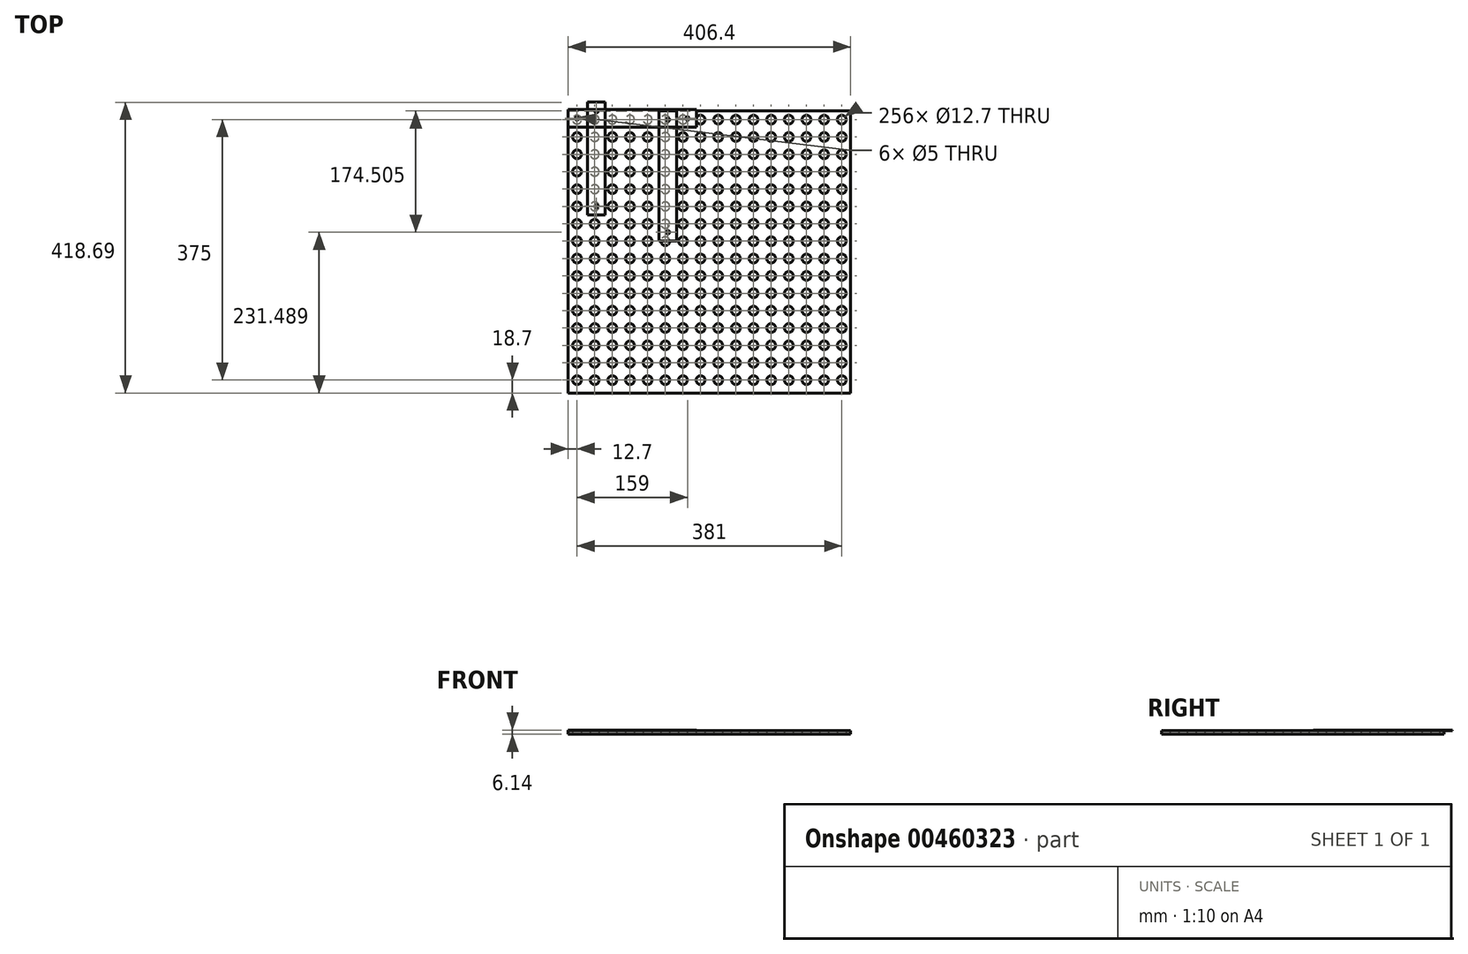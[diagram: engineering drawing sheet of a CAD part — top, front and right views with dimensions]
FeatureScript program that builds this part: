
annotation { "Feature Type Name" : "Feature", "Feature Type Description" : "" }
export const myFeature = defineFeature(function(context is Context, id is Id, definition is map)
    precondition{}
    {
        {
            var Q0;
            Q0=qCreatedBy(makeId("Top.planeOp"),FACE);
            var sketch = newSketch(context, id + "F0", { "sketchPlane" : qUnion([Q0])});
            skLineSegment(sketch, "E0.bottom", {"start": v(6.35, -6.35) * mm, "end": v(412.75, -6.35) * mm});
            skLineSegment(sketch, "E0.top", {"start": v(6.35, 400.05) * mm, "end": v(412.75, 400.05) * mm});
            skLineSegment(sketch, "E0.left", {"start": v(6.35, -6.35) * mm, "end": v(6.35, 400.05) * mm});
            skLineSegment(sketch, "E0.right", {"start": v(412.75, -6.35) * mm, "end": v(412.75, 400.05) * mm});
            skCircle(sketch, "E1", {"center": v(19.05, 387.35) * mm, "radius": 6.35 * mm});
            skLineSegment(sketch, "E2", {"start": v(19.05, 387.35) * mm, "end": v(19.05, 400.05) * mm, "construction": true});
            skLineSegment(sketch, "E3", {"start": v(19.05, 387.35) * mm, "end": v(6.35, 387.35) * mm, "construction": true});
            skCircle(sketch, "E4.0.1.0", {"center": v(19.05, 362.35) * mm, "radius": 6.35 * mm});
            skCircle(sketch, "E4.0.2.0", {"center": v(19.05, 337.35) * mm, "radius": 6.35 * mm});
            skCircle(sketch, "E4.0.3.0", {"center": v(19.05, 312.35) * mm, "radius": 6.35 * mm});
            skCircle(sketch, "E4.0.4.0", {"center": v(19.05, 287.35) * mm, "radius": 6.35 * mm});
            skCircle(sketch, "E4.0.5.0", {"center": v(19.05, 262.35) * mm, "radius": 6.35 * mm});
            skCircle(sketch, "E4.0.6.0", {"center": v(19.05, 237.35) * mm, "radius": 6.35 * mm});
            skCircle(sketch, "E4.0.7.0", {"center": v(19.05, 212.35) * mm, "radius": 6.35 * mm});
            skCircle(sketch, "E4.0.8.0", {"center": v(19.05, 187.35) * mm, "radius": 6.35 * mm});
            skCircle(sketch, "E4.0.9.0", {"center": v(19.05, 162.35) * mm, "radius": 6.35 * mm});
            skCircle(sketch, "E4.0.10.0", {"center": v(19.05, 137.35) * mm, "radius": 6.35 * mm});
            skCircle(sketch, "E4.0.11.0", {"center": v(19.05, 112.35) * mm, "radius": 6.35 * mm});
            skCircle(sketch, "E4.0.12.0", {"center": v(19.05, 87.35) * mm, "radius": 6.35 * mm});
            skCircle(sketch, "E4.0.13.0", {"center": v(19.05, 62.35) * mm, "radius": 6.35 * mm});
            skCircle(sketch, "E4.0.14.0", {"center": v(19.05, 37.35) * mm, "radius": 6.35 * mm});
            skCircle(sketch, "E4.1.0.0", {"center": v(44.45, 387.35) * mm, "radius": 6.35 * mm});
            skCircle(sketch, "E4.1.1.0", {"center": v(44.45, 362.35) * mm, "radius": 6.35 * mm});
            skCircle(sketch, "E4.1.2.0", {"center": v(44.45, 337.35) * mm, "radius": 6.35 * mm});
            skCircle(sketch, "E4.1.3.0", {"center": v(44.45, 312.35) * mm, "radius": 6.35 * mm});
            skCircle(sketch, "E4.1.4.0", {"center": v(44.45, 287.35) * mm, "radius": 6.35 * mm});
            skCircle(sketch, "E4.1.5.0", {"center": v(44.45, 262.35) * mm, "radius": 6.35 * mm});
            skCircle(sketch, "E4.1.6.0", {"center": v(44.45, 237.35) * mm, "radius": 6.35 * mm});
            skCircle(sketch, "E4.1.7.0", {"center": v(44.45, 212.35) * mm, "radius": 6.35 * mm});
            skCircle(sketch, "E4.1.8.0", {"center": v(44.45, 187.35) * mm, "radius": 6.35 * mm});
            skCircle(sketch, "E4.1.9.0", {"center": v(44.45, 162.35) * mm, "radius": 6.35 * mm});
            skCircle(sketch, "E4.1.10.0", {"center": v(44.45, 137.35) * mm, "radius": 6.35 * mm});
            skCircle(sketch, "E4.1.11.0", {"center": v(44.45, 112.35) * mm, "radius": 6.35 * mm});
            skCircle(sketch, "E4.1.12.0", {"center": v(44.45, 87.35) * mm, "radius": 6.35 * mm});
            skCircle(sketch, "E4.1.13.0", {"center": v(44.45, 62.35) * mm, "radius": 6.35 * mm});
            skCircle(sketch, "E4.1.14.0", {"center": v(44.45, 37.35) * mm, "radius": 6.35 * mm});
            skCircle(sketch, "E4.2.0.0", {"center": v(69.85, 387.35) * mm, "radius": 6.35 * mm});
            skCircle(sketch, "E4.2.1.0", {"center": v(69.85, 362.35) * mm, "radius": 6.35 * mm});
            skCircle(sketch, "E4.2.2.0", {"center": v(69.85, 337.35) * mm, "radius": 6.35 * mm});
            skCircle(sketch, "E4.2.3.0", {"center": v(69.85, 312.35) * mm, "radius": 6.35 * mm});
            skCircle(sketch, "E4.2.4.0", {"center": v(69.85, 287.35) * mm, "radius": 6.35 * mm});
            skCircle(sketch, "E4.2.5.0", {"center": v(69.85, 262.35) * mm, "radius": 6.35 * mm});
            skCircle(sketch, "E4.2.6.0", {"center": v(69.85, 237.35) * mm, "radius": 6.35 * mm});
            skCircle(sketch, "E4.2.7.0", {"center": v(69.85, 212.35) * mm, "radius": 6.35 * mm});
            skCircle(sketch, "E4.2.8.0", {"center": v(69.85, 187.35) * mm, "radius": 6.35 * mm});
            skCircle(sketch, "E4.2.9.0", {"center": v(69.85, 162.35) * mm, "radius": 6.35 * mm});
            skCircle(sketch, "E4.2.10.0", {"center": v(69.85, 137.35) * mm, "radius": 6.35 * mm});
            skCircle(sketch, "E4.2.11.0", {"center": v(69.85, 112.35) * mm, "radius": 6.35 * mm});
            skCircle(sketch, "E4.2.12.0", {"center": v(69.85, 87.35) * mm, "radius": 6.35 * mm});
            skCircle(sketch, "E4.2.13.0", {"center": v(69.85, 62.35) * mm, "radius": 6.35 * mm});
            skCircle(sketch, "E4.2.14.0", {"center": v(69.85, 37.35) * mm, "radius": 6.35 * mm});
            skCircle(sketch, "E4.3.0.0", {"center": v(95.25, 387.35) * mm, "radius": 6.35 * mm});
            skCircle(sketch, "E4.3.1.0", {"center": v(95.25, 362.35) * mm, "radius": 6.35 * mm});
            skCircle(sketch, "E4.3.2.0", {"center": v(95.25, 337.35) * mm, "radius": 6.35 * mm});
            skCircle(sketch, "E4.3.3.0", {"center": v(95.25, 312.35) * mm, "radius": 6.35 * mm});
            skCircle(sketch, "E4.3.4.0", {"center": v(95.25, 287.35) * mm, "radius": 6.35 * mm});
            skCircle(sketch, "E4.3.5.0", {"center": v(95.25, 262.35) * mm, "radius": 6.35 * mm});
            skCircle(sketch, "E4.3.6.0", {"center": v(95.25, 237.35) * mm, "radius": 6.35 * mm});
            skCircle(sketch, "E4.3.7.0", {"center": v(95.25, 212.35) * mm, "radius": 6.35 * mm});
            skCircle(sketch, "E4.3.8.0", {"center": v(95.25, 187.35) * mm, "radius": 6.35 * mm});
            skCircle(sketch, "E4.3.9.0", {"center": v(95.25, 162.35) * mm, "radius": 6.35 * mm});
            skCircle(sketch, "E4.3.10.0", {"center": v(95.25, 137.35) * mm, "radius": 6.35 * mm});
            skCircle(sketch, "E4.3.11.0", {"center": v(95.25, 112.35) * mm, "radius": 6.35 * mm});
            skCircle(sketch, "E4.3.12.0", {"center": v(95.25, 87.35) * mm, "radius": 6.35 * mm});
            skCircle(sketch, "E4.3.13.0", {"center": v(95.25, 62.35) * mm, "radius": 6.35 * mm});
            skCircle(sketch, "E4.3.14.0", {"center": v(95.25, 37.35) * mm, "radius": 6.35 * mm});
            skCircle(sketch, "E4.4.0.0", {"center": v(120.65, 387.35) * mm, "radius": 6.35 * mm});
            skCircle(sketch, "E4.4.1.0", {"center": v(120.65, 362.35) * mm, "radius": 6.35 * mm});
            skCircle(sketch, "E4.4.2.0", {"center": v(120.65, 337.35) * mm, "radius": 6.35 * mm});
            skCircle(sketch, "E4.4.3.0", {"center": v(120.65, 312.35) * mm, "radius": 6.35 * mm});
            skCircle(sketch, "E4.4.4.0", {"center": v(120.65, 287.35) * mm, "radius": 6.35 * mm});
            skCircle(sketch, "E4.4.5.0", {"center": v(120.65, 262.35) * mm, "radius": 6.35 * mm});
            skCircle(sketch, "E4.4.6.0", {"center": v(120.65, 237.35) * mm, "radius": 6.35 * mm});
            skCircle(sketch, "E4.4.7.0", {"center": v(120.65, 212.35) * mm, "radius": 6.35 * mm});
            skCircle(sketch, "E4.4.8.0", {"center": v(120.65, 187.35) * mm, "radius": 6.35 * mm});
            skCircle(sketch, "E4.4.9.0", {"center": v(120.65, 162.35) * mm, "radius": 6.35 * mm});
            skCircle(sketch, "E4.4.10.0", {"center": v(120.65, 137.35) * mm, "radius": 6.35 * mm});
            skCircle(sketch, "E4.4.11.0", {"center": v(120.65, 112.35) * mm, "radius": 6.35 * mm});
            skCircle(sketch, "E4.4.12.0", {"center": v(120.65, 87.35) * mm, "radius": 6.35 * mm});
            skCircle(sketch, "E4.4.13.0", {"center": v(120.65, 62.35) * mm, "radius": 6.35 * mm});
            skCircle(sketch, "E4.4.14.0", {"center": v(120.65, 37.35) * mm, "radius": 6.35 * mm});
            skCircle(sketch, "E4.5.0.0", {"center": v(146.05, 387.35) * mm, "radius": 6.35 * mm});
            skCircle(sketch, "E4.5.1.0", {"center": v(146.05, 362.35) * mm, "radius": 6.35 * mm});
            skCircle(sketch, "E4.5.2.0", {"center": v(146.05, 337.35) * mm, "radius": 6.35 * mm});
            skCircle(sketch, "E4.5.3.0", {"center": v(146.05, 312.35) * mm, "radius": 6.35 * mm});
            skCircle(sketch, "E4.5.4.0", {"center": v(146.05, 287.35) * mm, "radius": 6.35 * mm});
            skCircle(sketch, "E4.5.5.0", {"center": v(146.05, 262.35) * mm, "radius": 6.35 * mm});
            skCircle(sketch, "E4.5.6.0", {"center": v(146.05, 237.35) * mm, "radius": 6.35 * mm});
            skCircle(sketch, "E4.5.7.0", {"center": v(146.05, 212.35) * mm, "radius": 6.35 * mm});
            skCircle(sketch, "E4.5.8.0", {"center": v(146.05, 187.35) * mm, "radius": 6.35 * mm});
            skCircle(sketch, "E4.5.9.0", {"center": v(146.05, 162.35) * mm, "radius": 6.35 * mm});
            skCircle(sketch, "E4.5.10.0", {"center": v(146.05, 137.35) * mm, "radius": 6.35 * mm});
            skCircle(sketch, "E4.5.11.0", {"center": v(146.05, 112.35) * mm, "radius": 6.35 * mm});
            skCircle(sketch, "E4.5.12.0", {"center": v(146.05, 87.35) * mm, "radius": 6.35 * mm});
            skCircle(sketch, "E4.5.13.0", {"center": v(146.05, 62.35) * mm, "radius": 6.35 * mm});
            skCircle(sketch, "E4.5.14.0", {"center": v(146.05, 37.35) * mm, "radius": 6.35 * mm});
            skCircle(sketch, "E4.6.0.0", {"center": v(171.45, 387.35) * mm, "radius": 6.35 * mm});
            skCircle(sketch, "E4.6.1.0", {"center": v(171.45, 362.35) * mm, "radius": 6.35 * mm});
            skCircle(sketch, "E4.6.2.0", {"center": v(171.45, 337.35) * mm, "radius": 6.35 * mm});
            skCircle(sketch, "E4.6.3.0", {"center": v(171.45, 312.35) * mm, "radius": 6.35 * mm});
            skCircle(sketch, "E4.6.4.0", {"center": v(171.45, 287.35) * mm, "radius": 6.35 * mm});
            skCircle(sketch, "E4.6.5.0", {"center": v(171.45, 262.35) * mm, "radius": 6.35 * mm});
            skCircle(sketch, "E4.6.6.0", {"center": v(171.45, 237.35) * mm, "radius": 6.35 * mm});
            skCircle(sketch, "E4.6.7.0", {"center": v(171.45, 212.35) * mm, "radius": 6.35 * mm});
            skCircle(sketch, "E4.6.8.0", {"center": v(171.45, 187.35) * mm, "radius": 6.35 * mm});
            skCircle(sketch, "E4.6.9.0", {"center": v(171.45, 162.35) * mm, "radius": 6.35 * mm});
            skCircle(sketch, "E4.6.10.0", {"center": v(171.45, 137.35) * mm, "radius": 6.35 * mm});
            skCircle(sketch, "E4.6.11.0", {"center": v(171.45, 112.35) * mm, "radius": 6.35 * mm});
            skCircle(sketch, "E4.6.12.0", {"center": v(171.45, 87.35) * mm, "radius": 6.35 * mm});
            skCircle(sketch, "E4.6.13.0", {"center": v(171.45, 62.35) * mm, "radius": 6.35 * mm});
            skCircle(sketch, "E4.6.14.0", {"center": v(171.45, 37.35) * mm, "radius": 6.35 * mm});
            skCircle(sketch, "E4.7.0.0", {"center": v(196.85, 387.35) * mm, "radius": 6.35 * mm});
            skCircle(sketch, "E4.7.1.0", {"center": v(196.85, 362.35) * mm, "radius": 6.35 * mm});
            skCircle(sketch, "E4.7.2.0", {"center": v(196.85, 337.35) * mm, "radius": 6.35 * mm});
            skCircle(sketch, "E4.7.3.0", {"center": v(196.85, 312.35) * mm, "radius": 6.35 * mm});
            skCircle(sketch, "E4.7.4.0", {"center": v(196.85, 287.35) * mm, "radius": 6.35 * mm});
            skCircle(sketch, "E4.7.5.0", {"center": v(196.85, 262.35) * mm, "radius": 6.35 * mm});
            skCircle(sketch, "E4.7.6.0", {"center": v(196.85, 237.35) * mm, "radius": 6.35 * mm});
            skCircle(sketch, "E4.7.7.0", {"center": v(196.85, 212.35) * mm, "radius": 6.35 * mm});
            skCircle(sketch, "E4.7.8.0", {"center": v(196.85, 187.35) * mm, "radius": 6.35 * mm});
            skCircle(sketch, "E4.7.9.0", {"center": v(196.85, 162.35) * mm, "radius": 6.35 * mm});
            skCircle(sketch, "E4.7.10.0", {"center": v(196.85, 137.35) * mm, "radius": 6.35 * mm});
            skCircle(sketch, "E4.7.11.0", {"center": v(196.85, 112.35) * mm, "radius": 6.35 * mm});
            skCircle(sketch, "E4.7.12.0", {"center": v(196.85, 87.35) * mm, "radius": 6.35 * mm});
            skCircle(sketch, "E4.7.13.0", {"center": v(196.85, 62.35) * mm, "radius": 6.35 * mm});
            skCircle(sketch, "E4.7.14.0", {"center": v(196.85, 37.35) * mm, "radius": 6.35 * mm});
            skCircle(sketch, "E4.8.0.0", {"center": v(222.25, 387.35) * mm, "radius": 6.35 * mm});
            skCircle(sketch, "E4.8.1.0", {"center": v(222.25, 362.35) * mm, "radius": 6.35 * mm});
            skCircle(sketch, "E4.8.2.0", {"center": v(222.25, 337.35) * mm, "radius": 6.35 * mm});
            skCircle(sketch, "E4.8.3.0", {"center": v(222.25, 312.35) * mm, "radius": 6.35 * mm});
            skCircle(sketch, "E4.8.4.0", {"center": v(222.25, 287.35) * mm, "radius": 6.35 * mm});
            skCircle(sketch, "E4.8.5.0", {"center": v(222.25, 262.35) * mm, "radius": 6.35 * mm});
            skCircle(sketch, "E4.8.6.0", {"center": v(222.25, 237.35) * mm, "radius": 6.35 * mm});
            skCircle(sketch, "E4.8.7.0", {"center": v(222.25, 212.35) * mm, "radius": 6.35 * mm});
            skCircle(sketch, "E4.8.8.0", {"center": v(222.25, 187.35) * mm, "radius": 6.35 * mm});
            skCircle(sketch, "E4.8.9.0", {"center": v(222.25, 162.35) * mm, "radius": 6.35 * mm});
            skCircle(sketch, "E4.8.10.0", {"center": v(222.25, 137.35) * mm, "radius": 6.35 * mm});
            skCircle(sketch, "E4.8.11.0", {"center": v(222.25, 112.35) * mm, "radius": 6.35 * mm});
            skCircle(sketch, "E4.8.12.0", {"center": v(222.25, 87.35) * mm, "radius": 6.35 * mm});
            skCircle(sketch, "E4.8.13.0", {"center": v(222.25, 62.35) * mm, "radius": 6.35 * mm});
            skCircle(sketch, "E4.8.14.0", {"center": v(222.25, 37.35) * mm, "radius": 6.35 * mm});
            skCircle(sketch, "E4.9.0.0", {"center": v(247.65, 387.35) * mm, "radius": 6.35 * mm});
            skCircle(sketch, "E4.9.1.0", {"center": v(247.65, 362.35) * mm, "radius": 6.35 * mm});
            skCircle(sketch, "E4.9.2.0", {"center": v(247.65, 337.35) * mm, "radius": 6.35 * mm});
            skCircle(sketch, "E4.9.3.0", {"center": v(247.65, 312.35) * mm, "radius": 6.35 * mm});
            skCircle(sketch, "E4.9.4.0", {"center": v(247.65, 287.35) * mm, "radius": 6.35 * mm});
            skCircle(sketch, "E4.9.5.0", {"center": v(247.65, 262.35) * mm, "radius": 6.35 * mm});
            skCircle(sketch, "E4.9.6.0", {"center": v(247.65, 237.35) * mm, "radius": 6.35 * mm});
            skCircle(sketch, "E4.9.7.0", {"center": v(247.65, 212.35) * mm, "radius": 6.35 * mm});
            skCircle(sketch, "E4.9.8.0", {"center": v(247.65, 187.35) * mm, "radius": 6.35 * mm});
            skCircle(sketch, "E4.9.9.0", {"center": v(247.65, 162.35) * mm, "radius": 6.35 * mm});
            skCircle(sketch, "E4.9.10.0", {"center": v(247.65, 137.35) * mm, "radius": 6.35 * mm});
            skCircle(sketch, "E4.9.11.0", {"center": v(247.65, 112.35) * mm, "radius": 6.35 * mm});
            skCircle(sketch, "E4.9.12.0", {"center": v(247.65, 87.35) * mm, "radius": 6.35 * mm});
            skCircle(sketch, "E4.9.13.0", {"center": v(247.65, 62.35) * mm, "radius": 6.35 * mm});
            skCircle(sketch, "E4.9.14.0", {"center": v(247.65, 37.35) * mm, "radius": 6.35 * mm});
            skCircle(sketch, "E4.10.0.0", {"center": v(273.05, 387.35) * mm, "radius": 6.35 * mm});
            skCircle(sketch, "E4.10.1.0", {"center": v(273.05, 362.35) * mm, "radius": 6.35 * mm});
            skCircle(sketch, "E4.10.2.0", {"center": v(273.05, 337.35) * mm, "radius": 6.35 * mm});
            skCircle(sketch, "E4.10.3.0", {"center": v(273.05, 312.35) * mm, "radius": 6.35 * mm});
            skCircle(sketch, "E4.10.4.0", {"center": v(273.05, 287.35) * mm, "radius": 6.35 * mm});
            skCircle(sketch, "E4.10.5.0", {"center": v(273.05, 262.35) * mm, "radius": 6.35 * mm});
            skCircle(sketch, "E4.10.6.0", {"center": v(273.05, 237.35) * mm, "radius": 6.35 * mm});
            skCircle(sketch, "E4.10.7.0", {"center": v(273.05, 212.35) * mm, "radius": 6.35 * mm});
            skCircle(sketch, "E4.10.8.0", {"center": v(273.05, 187.35) * mm, "radius": 6.35 * mm});
            skCircle(sketch, "E4.10.9.0", {"center": v(273.05, 162.35) * mm, "radius": 6.35 * mm});
            skCircle(sketch, "E4.10.10.0", {"center": v(273.05, 137.35) * mm, "radius": 6.35 * mm});
            skCircle(sketch, "E4.10.11.0", {"center": v(273.05, 112.35) * mm, "radius": 6.35 * mm});
            skCircle(sketch, "E4.10.12.0", {"center": v(273.05, 87.35) * mm, "radius": 6.35 * mm});
            skCircle(sketch, "E4.10.13.0", {"center": v(273.05, 62.35) * mm, "radius": 6.35 * mm});
            skCircle(sketch, "E4.10.14.0", {"center": v(273.05, 37.35) * mm, "radius": 6.35 * mm});
            skCircle(sketch, "E4.11.0.0", {"center": v(298.45, 387.35) * mm, "radius": 6.35 * mm});
            skCircle(sketch, "E4.11.1.0", {"center": v(298.45, 362.35) * mm, "radius": 6.35 * mm});
            skCircle(sketch, "E4.11.2.0", {"center": v(298.45, 337.35) * mm, "radius": 6.35 * mm});
            skCircle(sketch, "E4.11.3.0", {"center": v(298.45, 312.35) * mm, "radius": 6.35 * mm});
            skCircle(sketch, "E4.11.4.0", {"center": v(298.45, 287.35) * mm, "radius": 6.35 * mm});
            skCircle(sketch, "E4.11.5.0", {"center": v(298.45, 262.35) * mm, "radius": 6.35 * mm});
            skCircle(sketch, "E4.11.6.0", {"center": v(298.45, 237.35) * mm, "radius": 6.35 * mm});
            skCircle(sketch, "E4.11.7.0", {"center": v(298.45, 212.35) * mm, "radius": 6.35 * mm});
            skCircle(sketch, "E4.11.8.0", {"center": v(298.45, 187.35) * mm, "radius": 6.35 * mm});
            skCircle(sketch, "E4.11.9.0", {"center": v(298.45, 162.35) * mm, "radius": 6.35 * mm});
            skCircle(sketch, "E4.11.10.0", {"center": v(298.45, 137.35) * mm, "radius": 6.35 * mm});
            skCircle(sketch, "E4.11.11.0", {"center": v(298.45, 112.35) * mm, "radius": 6.35 * mm});
            skCircle(sketch, "E4.11.12.0", {"center": v(298.45, 87.35) * mm, "radius": 6.35 * mm});
            skCircle(sketch, "E4.11.13.0", {"center": v(298.45, 62.35) * mm, "radius": 6.35 * mm});
            skCircle(sketch, "E4.11.14.0", {"center": v(298.45, 37.35) * mm, "radius": 6.35 * mm});
            skCircle(sketch, "E4.12.0.0", {"center": v(323.85, 387.35) * mm, "radius": 6.35 * mm});
            skCircle(sketch, "E4.12.1.0", {"center": v(323.85, 362.35) * mm, "radius": 6.35 * mm});
            skCircle(sketch, "E4.12.2.0", {"center": v(323.85, 337.35) * mm, "radius": 6.35 * mm});
            skCircle(sketch, "E4.12.3.0", {"center": v(323.85, 312.35) * mm, "radius": 6.35 * mm});
            skCircle(sketch, "E4.12.4.0", {"center": v(323.85, 287.35) * mm, "radius": 6.35 * mm});
            skCircle(sketch, "E4.12.5.0", {"center": v(323.85, 262.35) * mm, "radius": 6.35 * mm});
            skCircle(sketch, "E4.12.6.0", {"center": v(323.85, 237.35) * mm, "radius": 6.35 * mm});
            skCircle(sketch, "E4.12.7.0", {"center": v(323.85, 212.35) * mm, "radius": 6.35 * mm});
            skCircle(sketch, "E4.12.8.0", {"center": v(323.85, 187.35) * mm, "radius": 6.35 * mm});
            skCircle(sketch, "E4.12.9.0", {"center": v(323.85, 162.35) * mm, "radius": 6.35 * mm});
            skCircle(sketch, "E4.12.10.0", {"center": v(323.85, 137.35) * mm, "radius": 6.35 * mm});
            skCircle(sketch, "E4.12.11.0", {"center": v(323.85, 112.35) * mm, "radius": 6.35 * mm});
            skCircle(sketch, "E4.12.12.0", {"center": v(323.85, 87.35) * mm, "radius": 6.35 * mm});
            skCircle(sketch, "E4.12.13.0", {"center": v(323.85, 62.35) * mm, "radius": 6.35 * mm});
            skCircle(sketch, "E4.12.14.0", {"center": v(323.85, 37.35) * mm, "radius": 6.35 * mm});
            skCircle(sketch, "E4.13.0.0", {"center": v(349.25, 387.35) * mm, "radius": 6.35 * mm});
            skCircle(sketch, "E4.13.1.0", {"center": v(349.25, 362.35) * mm, "radius": 6.35 * mm});
            skCircle(sketch, "E4.13.2.0", {"center": v(349.25, 337.35) * mm, "radius": 6.35 * mm});
            skCircle(sketch, "E4.13.3.0", {"center": v(349.25, 312.35) * mm, "radius": 6.35 * mm});
            skCircle(sketch, "E4.13.4.0", {"center": v(349.25, 287.35) * mm, "radius": 6.35 * mm});
            skCircle(sketch, "E4.13.5.0", {"center": v(349.25, 262.35) * mm, "radius": 6.35 * mm});
            skCircle(sketch, "E4.13.6.0", {"center": v(349.25, 237.35) * mm, "radius": 6.35 * mm});
            skCircle(sketch, "E4.13.7.0", {"center": v(349.25, 212.35) * mm, "radius": 6.35 * mm});
            skCircle(sketch, "E4.13.8.0", {"center": v(349.25, 187.35) * mm, "radius": 6.35 * mm});
            skCircle(sketch, "E4.13.9.0", {"center": v(349.25, 162.35) * mm, "radius": 6.35 * mm});
            skCircle(sketch, "E4.13.10.0", {"center": v(349.25, 137.35) * mm, "radius": 6.35 * mm});
            skCircle(sketch, "E4.13.11.0", {"center": v(349.25, 112.35) * mm, "radius": 6.35 * mm});
            skCircle(sketch, "E4.13.12.0", {"center": v(349.25, 87.35) * mm, "radius": 6.35 * mm});
            skCircle(sketch, "E4.13.13.0", {"center": v(349.25, 62.35) * mm, "radius": 6.35 * mm});
            skCircle(sketch, "E4.13.14.0", {"center": v(349.25, 37.35) * mm, "radius": 6.35 * mm});
            skCircle(sketch, "E4.14.0.0", {"center": v(374.65, 387.35) * mm, "radius": 6.35 * mm});
            skCircle(sketch, "E4.14.1.0", {"center": v(374.65, 362.35) * mm, "radius": 6.35 * mm});
            skCircle(sketch, "E4.14.2.0", {"center": v(374.65, 337.35) * mm, "radius": 6.35 * mm});
            skCircle(sketch, "E4.14.3.0", {"center": v(374.65, 312.35) * mm, "radius": 6.35 * mm});
            skCircle(sketch, "E4.14.4.0", {"center": v(374.65, 287.35) * mm, "radius": 6.35 * mm});
            skCircle(sketch, "E4.14.5.0", {"center": v(374.65, 262.35) * mm, "radius": 6.35 * mm});
            skCircle(sketch, "E4.14.6.0", {"center": v(374.65, 237.35) * mm, "radius": 6.35 * mm});
            skCircle(sketch, "E4.14.7.0", {"center": v(374.65, 212.35) * mm, "radius": 6.35 * mm});
            skCircle(sketch, "E4.14.8.0", {"center": v(374.65, 187.35) * mm, "radius": 6.35 * mm});
            skCircle(sketch, "E4.14.9.0", {"center": v(374.65, 162.35) * mm, "radius": 6.35 * mm});
            skCircle(sketch, "E4.14.10.0", {"center": v(374.65, 137.35) * mm, "radius": 6.35 * mm});
            skCircle(sketch, "E4.14.11.0", {"center": v(374.65, 112.35) * mm, "radius": 6.35 * mm});
            skCircle(sketch, "E4.14.12.0", {"center": v(374.65, 87.35) * mm, "radius": 6.35 * mm});
            skCircle(sketch, "E4.14.13.0", {"center": v(374.65, 62.35) * mm, "radius": 6.35 * mm});
            skCircle(sketch, "E4.14.14.0", {"center": v(374.65, 37.35) * mm, "radius": 6.35 * mm});
            skLineSegment(sketch, "E4.direction1", {"start": v(19.05, 387.35) * mm, "end": v(44.45, 387.35) * mm, "construction": true});
            skLineSegment(sketch, "E4.direction2", {"start": v(19.05, 387.35) * mm, "end": v(19.05, 362.35) * mm, "construction": true});
            skCircle(sketch, "E5.0.15.0", {"center": v(400.05, 387.35) * mm, "radius": 6.35 * mm});
            skCircle(sketch, "E5.0.15.1", {"center": v(400.05, 362.35) * mm, "radius": 6.35 * mm});
            skCircle(sketch, "E5.0.15.2", {"center": v(400.05, 337.35) * mm, "radius": 6.35 * mm});
            skCircle(sketch, "E5.0.15.3", {"center": v(400.05, 312.35) * mm, "radius": 6.35 * mm});
            skCircle(sketch, "E5.0.15.4", {"center": v(400.05, 287.35) * mm, "radius": 6.35 * mm});
            skCircle(sketch, "E5.0.15.5", {"center": v(400.05, 262.35) * mm, "radius": 6.35 * mm});
            skCircle(sketch, "E5.0.15.6", {"center": v(400.05, 237.35) * mm, "radius": 6.35 * mm});
            skCircle(sketch, "E5.0.15.7", {"center": v(400.05, 212.35) * mm, "radius": 6.35 * mm});
            skCircle(sketch, "E5.0.15.8", {"center": v(400.05, 187.35) * mm, "radius": 6.35 * mm});
            skCircle(sketch, "E5.0.15.9", {"center": v(400.05, 162.35) * mm, "radius": 6.35 * mm});
            skCircle(sketch, "E5.0.15.10", {"center": v(400.05, 137.35) * mm, "radius": 6.35 * mm});
            skCircle(sketch, "E5.0.15.11", {"center": v(400.05, 112.35) * mm, "radius": 6.35 * mm});
            skCircle(sketch, "E5.0.15.12", {"center": v(400.05, 87.35) * mm, "radius": 6.35 * mm});
            skCircle(sketch, "E5.0.15.13", {"center": v(400.05, 62.35) * mm, "radius": 6.35 * mm});
            skCircle(sketch, "E5.0.15.14", {"center": v(400.05, 37.35) * mm, "radius": 6.35 * mm});
            skCircle(sketch, "E6.0.0.15", {"center": v(19.05, 12.35) * mm, "radius": 6.35 * mm});
            skCircle(sketch, "E6.0.1.15", {"center": v(44.45, 12.35) * mm, "radius": 6.35 * mm});
            skCircle(sketch, "E6.0.2.15", {"center": v(69.85, 12.35) * mm, "radius": 6.35 * mm});
            skCircle(sketch, "E6.0.3.15", {"center": v(95.25, 12.35) * mm, "radius": 6.35 * mm});
            skCircle(sketch, "E6.0.4.15", {"center": v(120.65, 12.35) * mm, "radius": 6.35 * mm});
            skCircle(sketch, "E6.0.5.15", {"center": v(146.05, 12.35) * mm, "radius": 6.35 * mm});
            skCircle(sketch, "E6.0.6.15", {"center": v(171.45, 12.35) * mm, "radius": 6.35 * mm});
            skCircle(sketch, "E6.0.7.15", {"center": v(196.85, 12.35) * mm, "radius": 6.35 * mm});
            skCircle(sketch, "E6.0.8.15", {"center": v(222.25, 12.35) * mm, "radius": 6.35 * mm});
            skCircle(sketch, "E6.0.9.15", {"center": v(247.65, 12.35) * mm, "radius": 6.35 * mm});
            skCircle(sketch, "E6.0.10.15", {"center": v(273.05, 12.35) * mm, "radius": 6.35 * mm});
            skCircle(sketch, "E6.0.11.15", {"center": v(298.45, 12.35) * mm, "radius": 6.35 * mm});
            skCircle(sketch, "E6.0.12.15", {"center": v(323.85, 12.35) * mm, "radius": 6.35 * mm});
            skCircle(sketch, "E6.0.13.15", {"center": v(349.25, 12.35) * mm, "radius": 6.35 * mm});
            skCircle(sketch, "E6.0.14.15", {"center": v(374.65, 12.35) * mm, "radius": 6.35 * mm});
            skCircle(sketch, "E6.0.15.15", {"center": v(400.05, 12.35) * mm, "radius": 6.35 * mm});
            skSolve(sketch);
        }
        {
            var Q0;
            Q0 = qSketchRegion(id + "F0", true);
            extrude(context, id + "F1", {"entities" : qUnion([Q0]), "depth" : 5 * mm});
        }
        {
            var Q0;
            Q0=makeQuery(id+"F1.opExtrude","CAP_FACE",FACE,{"disambiguationData":[OSD([sQuery(id+"F0.wireOp",EDGE,"E0.bottom"),sQuery(id+"F0.wireOp",EDGE,"E0.top"),sQuery(id+"F0.wireOp",EDGE,"E0.left"),sQuery(id+"F0.wireOp",EDGE,"E0.right"),sQuery(id+"F0.wireOp",EDGE,"E1"),sQuery(id+"F0.wireOp",EDGE,"E4.0.1.0"),sQuery(id+"F0.wireOp",EDGE,"E4.0.2.0"),sQuery(id+"F0.wireOp",EDGE,"E4.0.3.0"),sQuery(id+"F0.wireOp",EDGE,"E4.0.4.0"),sQuery(id+"F0.wireOp",EDGE,"E4.0.5.0"),sQuery(id+"F0.wireOp",EDGE,"E4.0.6.0"),sQuery(id+"F0.wireOp",EDGE,"E4.0.7.0"),sQuery(id+"F0.wireOp",EDGE,"E4.0.8.0"),sQuery(id+"F0.wireOp",EDGE,"E4.0.9.0"),sQuery(id+"F0.wireOp",EDGE,"E4.0.10.0"),sQuery(id+"F0.wireOp",EDGE,"E4.0.11.0"),sQuery(id+"F0.wireOp",EDGE,"E4.0.12.0"),sQuery(id+"F0.wireOp",EDGE,"E4.0.13.0"),sQuery(id+"F0.wireOp",EDGE,"E4.0.14.0"),sQuery(id+"F0.wireOp",EDGE,"E4.1.0.0"),sQuery(id+"F0.wireOp",EDGE,"E4.1.1.0"),sQuery(id+"F0.wireOp",EDGE,"E4.1.2.0"),sQuery(id+"F0.wireOp",EDGE,"E4.1.3.0"),sQuery(id+"F0.wireOp",EDGE,"E4.1.4.0"),sQuery(id+"F0.wireOp",EDGE,"E4.1.5.0"),sQuery(id+"F0.wireOp",EDGE,"E4.1.6.0"),sQuery(id+"F0.wireOp",EDGE,"E4.1.7.0"),sQuery(id+"F0.wireOp",EDGE,"E4.1.8.0"),sQuery(id+"F0.wireOp",EDGE,"E4.1.9.0"),sQuery(id+"F0.wireOp",EDGE,"E4.1.10.0"),sQuery(id+"F0.wireOp",EDGE,"E4.1.11.0"),sQuery(id+"F0.wireOp",EDGE,"E4.1.12.0"),sQuery(id+"F0.wireOp",EDGE,"E4.1.13.0"),sQuery(id+"F0.wireOp",EDGE,"E4.1.14.0"),sQuery(id+"F0.wireOp",EDGE,"E4.2.0.0"),sQuery(id+"F0.wireOp",EDGE,"E4.2.1.0"),sQuery(id+"F0.wireOp",EDGE,"E4.2.2.0"),sQuery(id+"F0.wireOp",EDGE,"E4.2.3.0"),sQuery(id+"F0.wireOp",EDGE,"E4.2.4.0"),sQuery(id+"F0.wireOp",EDGE,"E4.2.5.0"),sQuery(id+"F0.wireOp",EDGE,"E4.2.6.0"),sQuery(id+"F0.wireOp",EDGE,"E4.2.7.0"),sQuery(id+"F0.wireOp",EDGE,"E4.2.8.0"),sQuery(id+"F0.wireOp",EDGE,"E4.2.9.0"),sQuery(id+"F0.wireOp",EDGE,"E4.2.10.0"),sQuery(id+"F0.wireOp",EDGE,"E4.2.11.0"),sQuery(id+"F0.wireOp",EDGE,"E4.2.12.0"),sQuery(id+"F0.wireOp",EDGE,"E4.2.13.0"),sQuery(id+"F0.wireOp",EDGE,"E4.2.14.0"),sQuery(id+"F0.wireOp",EDGE,"E4.3.0.0"),sQuery(id+"F0.wireOp",EDGE,"E4.3.1.0"),sQuery(id+"F0.wireOp",EDGE,"E4.3.2.0"),sQuery(id+"F0.wireOp",EDGE,"E4.3.3.0"),sQuery(id+"F0.wireOp",EDGE,"E4.3.4.0"),sQuery(id+"F0.wireOp",EDGE,"E4.3.5.0"),sQuery(id+"F0.wireOp",EDGE,"E4.3.6.0"),sQuery(id+"F0.wireOp",EDGE,"E4.3.7.0"),sQuery(id+"F0.wireOp",EDGE,"E4.3.8.0"),sQuery(id+"F0.wireOp",EDGE,"E4.3.9.0"),sQuery(id+"F0.wireOp",EDGE,"E4.3.10.0"),sQuery(id+"F0.wireOp",EDGE,"E4.3.11.0"),sQuery(id+"F0.wireOp",EDGE,"E4.3.12.0"),sQuery(id+"F0.wireOp",EDGE,"E4.3.13.0"),sQuery(id+"F0.wireOp",EDGE,"E4.3.14.0"),sQuery(id+"F0.wireOp",EDGE,"E4.4.0.0"),sQuery(id+"F0.wireOp",EDGE,"E4.4.1.0"),sQuery(id+"F0.wireOp",EDGE,"E4.4.2.0"),sQuery(id+"F0.wireOp",EDGE,"E4.4.3.0"),sQuery(id+"F0.wireOp",EDGE,"E4.4.4.0"),sQuery(id+"F0.wireOp",EDGE,"E4.4.5.0"),sQuery(id+"F0.wireOp",EDGE,"E4.4.6.0"),sQuery(id+"F0.wireOp",EDGE,"E4.4.7.0"),sQuery(id+"F0.wireOp",EDGE,"E4.4.8.0"),sQuery(id+"F0.wireOp",EDGE,"E4.4.9.0"),sQuery(id+"F0.wireOp",EDGE,"E4.4.10.0"),sQuery(id+"F0.wireOp",EDGE,"E4.4.11.0"),sQuery(id+"F0.wireOp",EDGE,"E4.4.12.0"),sQuery(id+"F0.wireOp",EDGE,"E4.4.13.0"),sQuery(id+"F0.wireOp",EDGE,"E4.4.14.0"),sQuery(id+"F0.wireOp",EDGE,"E4.5.0.0"),sQuery(id+"F0.wireOp",EDGE,"E4.5.1.0"),sQuery(id+"F0.wireOp",EDGE,"E4.5.2.0"),sQuery(id+"F0.wireOp",EDGE,"E4.5.3.0"),sQuery(id+"F0.wireOp",EDGE,"E4.5.4.0"),sQuery(id+"F0.wireOp",EDGE,"E4.5.5.0"),sQuery(id+"F0.wireOp",EDGE,"E4.5.6.0"),sQuery(id+"F0.wireOp",EDGE,"E4.5.7.0"),sQuery(id+"F0.wireOp",EDGE,"E4.5.8.0"),sQuery(id+"F0.wireOp",EDGE,"E4.5.9.0"),sQuery(id+"F0.wireOp",EDGE,"E4.5.10.0"),sQuery(id+"F0.wireOp",EDGE,"E4.5.11.0"),sQuery(id+"F0.wireOp",EDGE,"E4.5.12.0"),sQuery(id+"F0.wireOp",EDGE,"E4.5.13.0"),sQuery(id+"F0.wireOp",EDGE,"E4.5.14.0"),sQuery(id+"F0.wireOp",EDGE,"E4.6.0.0"),sQuery(id+"F0.wireOp",EDGE,"E4.6.1.0"),sQuery(id+"F0.wireOp",EDGE,"E4.6.2.0"),sQuery(id+"F0.wireOp",EDGE,"E4.6.3.0"),sQuery(id+"F0.wireOp",EDGE,"E4.6.4.0"),sQuery(id+"F0.wireOp",EDGE,"E4.6.5.0"),sQuery(id+"F0.wireOp",EDGE,"E4.6.6.0"),sQuery(id+"F0.wireOp",EDGE,"E4.6.7.0"),sQuery(id+"F0.wireOp",EDGE,"E4.6.8.0"),sQuery(id+"F0.wireOp",EDGE,"E4.6.9.0"),sQuery(id+"F0.wireOp",EDGE,"E4.6.10.0"),sQuery(id+"F0.wireOp",EDGE,"E4.6.11.0"),sQuery(id+"F0.wireOp",EDGE,"E4.6.12.0"),sQuery(id+"F0.wireOp",EDGE,"E4.6.13.0"),sQuery(id+"F0.wireOp",EDGE,"E4.6.14.0"),sQuery(id+"F0.wireOp",EDGE,"E4.7.0.0"),sQuery(id+"F0.wireOp",EDGE,"E4.7.1.0"),sQuery(id+"F0.wireOp",EDGE,"E4.7.2.0"),sQuery(id+"F0.wireOp",EDGE,"E4.7.3.0"),sQuery(id+"F0.wireOp",EDGE,"E4.7.4.0"),sQuery(id+"F0.wireOp",EDGE,"E4.7.5.0"),sQuery(id+"F0.wireOp",EDGE,"E4.7.6.0"),sQuery(id+"F0.wireOp",EDGE,"E4.7.7.0"),sQuery(id+"F0.wireOp",EDGE,"E4.7.8.0"),sQuery(id+"F0.wireOp",EDGE,"E4.7.9.0"),sQuery(id+"F0.wireOp",EDGE,"E4.7.10.0"),sQuery(id+"F0.wireOp",EDGE,"E4.7.11.0"),sQuery(id+"F0.wireOp",EDGE,"E4.7.12.0"),sQuery(id+"F0.wireOp",EDGE,"E4.7.13.0"),sQuery(id+"F0.wireOp",EDGE,"E4.7.14.0"),sQuery(id+"F0.wireOp",EDGE,"E4.8.0.0"),sQuery(id+"F0.wireOp",EDGE,"E4.8.1.0"),sQuery(id+"F0.wireOp",EDGE,"E4.8.2.0"),sQuery(id+"F0.wireOp",EDGE,"E4.8.3.0"),sQuery(id+"F0.wireOp",EDGE,"E4.8.4.0"),sQuery(id+"F0.wireOp",EDGE,"E4.8.5.0"),sQuery(id+"F0.wireOp",EDGE,"E4.8.6.0"),sQuery(id+"F0.wireOp",EDGE,"E4.8.7.0"),sQuery(id+"F0.wireOp",EDGE,"E4.8.8.0"),sQuery(id+"F0.wireOp",EDGE,"E4.8.9.0"),sQuery(id+"F0.wireOp",EDGE,"E4.8.10.0"),sQuery(id+"F0.wireOp",EDGE,"E4.8.11.0"),sQuery(id+"F0.wireOp",EDGE,"E4.8.12.0"),sQuery(id+"F0.wireOp",EDGE,"E4.8.13.0"),sQuery(id+"F0.wireOp",EDGE,"E4.8.14.0"),sQuery(id+"F0.wireOp",EDGE,"E4.9.0.0"),sQuery(id+"F0.wireOp",EDGE,"E4.9.1.0"),sQuery(id+"F0.wireOp",EDGE,"E4.9.2.0"),sQuery(id+"F0.wireOp",EDGE,"E4.9.3.0"),sQuery(id+"F0.wireOp",EDGE,"E4.9.4.0"),sQuery(id+"F0.wireOp",EDGE,"E4.9.5.0"),sQuery(id+"F0.wireOp",EDGE,"E4.9.6.0"),sQuery(id+"F0.wireOp",EDGE,"E4.9.7.0"),sQuery(id+"F0.wireOp",EDGE,"E4.9.8.0"),sQuery(id+"F0.wireOp",EDGE,"E4.9.9.0"),sQuery(id+"F0.wireOp",EDGE,"E4.9.10.0"),sQuery(id+"F0.wireOp",EDGE,"E4.9.11.0"),sQuery(id+"F0.wireOp",EDGE,"E4.9.12.0"),sQuery(id+"F0.wireOp",EDGE,"E4.9.13.0"),sQuery(id+"F0.wireOp",EDGE,"E4.9.14.0"),sQuery(id+"F0.wireOp",EDGE,"E4.10.0.0"),sQuery(id+"F0.wireOp",EDGE,"E4.10.1.0"),sQuery(id+"F0.wireOp",EDGE,"E4.10.2.0"),sQuery(id+"F0.wireOp",EDGE,"E4.10.3.0"),sQuery(id+"F0.wireOp",EDGE,"E4.10.4.0"),sQuery(id+"F0.wireOp",EDGE,"E4.10.5.0"),sQuery(id+"F0.wireOp",EDGE,"E4.10.6.0"),sQuery(id+"F0.wireOp",EDGE,"E4.10.7.0"),sQuery(id+"F0.wireOp",EDGE,"E4.10.8.0"),sQuery(id+"F0.wireOp",EDGE,"E4.10.9.0"),sQuery(id+"F0.wireOp",EDGE,"E4.10.10.0"),sQuery(id+"F0.wireOp",EDGE,"E4.10.11.0"),sQuery(id+"F0.wireOp",EDGE,"E4.10.12.0"),sQuery(id+"F0.wireOp",EDGE,"E4.10.13.0"),sQuery(id+"F0.wireOp",EDGE,"E4.10.14.0"),sQuery(id+"F0.wireOp",EDGE,"E4.11.0.0"),sQuery(id+"F0.wireOp",EDGE,"E4.11.1.0"),sQuery(id+"F0.wireOp",EDGE,"E4.11.2.0"),sQuery(id+"F0.wireOp",EDGE,"E4.11.3.0"),sQuery(id+"F0.wireOp",EDGE,"E4.11.4.0"),sQuery(id+"F0.wireOp",EDGE,"E4.11.5.0"),sQuery(id+"F0.wireOp",EDGE,"E4.11.6.0"),sQuery(id+"F0.wireOp",EDGE,"E4.11.7.0"),sQuery(id+"F0.wireOp",EDGE,"E4.11.8.0"),sQuery(id+"F0.wireOp",EDGE,"E4.11.9.0"),sQuery(id+"F0.wireOp",EDGE,"E4.11.10.0"),sQuery(id+"F0.wireOp",EDGE,"E4.11.11.0"),sQuery(id+"F0.wireOp",EDGE,"E4.11.12.0"),sQuery(id+"F0.wireOp",EDGE,"E4.11.13.0"),sQuery(id+"F0.wireOp",EDGE,"E4.11.14.0"),sQuery(id+"F0.wireOp",EDGE,"E4.12.0.0"),sQuery(id+"F0.wireOp",EDGE,"E4.12.1.0"),sQuery(id+"F0.wireOp",EDGE,"E4.12.2.0"),sQuery(id+"F0.wireOp",EDGE,"E4.12.3.0"),sQuery(id+"F0.wireOp",EDGE,"E4.12.4.0"),sQuery(id+"F0.wireOp",EDGE,"E4.12.5.0"),sQuery(id+"F0.wireOp",EDGE,"E4.12.6.0"),sQuery(id+"F0.wireOp",EDGE,"E4.12.7.0"),sQuery(id+"F0.wireOp",EDGE,"E4.12.8.0"),sQuery(id+"F0.wireOp",EDGE,"E4.12.9.0"),sQuery(id+"F0.wireOp",EDGE,"E4.12.10.0"),sQuery(id+"F0.wireOp",EDGE,"E4.12.11.0"),sQuery(id+"F0.wireOp",EDGE,"E4.12.12.0"),sQuery(id+"F0.wireOp",EDGE,"E4.12.13.0"),sQuery(id+"F0.wireOp",EDGE,"E4.12.14.0"),sQuery(id+"F0.wireOp",EDGE,"E4.13.0.0"),sQuery(id+"F0.wireOp",EDGE,"E4.13.1.0"),sQuery(id+"F0.wireOp",EDGE,"E4.13.2.0"),sQuery(id+"F0.wireOp",EDGE,"E4.13.3.0"),sQuery(id+"F0.wireOp",EDGE,"E4.13.4.0"),sQuery(id+"F0.wireOp",EDGE,"E4.13.5.0"),sQuery(id+"F0.wireOp",EDGE,"E4.13.6.0"),sQuery(id+"F0.wireOp",EDGE,"E4.13.7.0"),sQuery(id+"F0.wireOp",EDGE,"E4.13.8.0"),sQuery(id+"F0.wireOp",EDGE,"E4.13.9.0"),sQuery(id+"F0.wireOp",EDGE,"E4.13.10.0"),sQuery(id+"F0.wireOp",EDGE,"E4.13.11.0"),sQuery(id+"F0.wireOp",EDGE,"E4.13.12.0"),sQuery(id+"F0.wireOp",EDGE,"E4.13.13.0"),sQuery(id+"F0.wireOp",EDGE,"E4.13.14.0"),sQuery(id+"F0.wireOp",EDGE,"E4.14.0.0"),sQuery(id+"F0.wireOp",EDGE,"E4.14.1.0"),sQuery(id+"F0.wireOp",EDGE,"E4.14.2.0"),sQuery(id+"F0.wireOp",EDGE,"E4.14.3.0"),sQuery(id+"F0.wireOp",EDGE,"E4.14.4.0"),sQuery(id+"F0.wireOp",EDGE,"E4.14.5.0"),sQuery(id+"F0.wireOp",EDGE,"E4.14.6.0"),sQuery(id+"F0.wireOp",EDGE,"E4.14.7.0"),sQuery(id+"F0.wireOp",EDGE,"E4.14.8.0"),sQuery(id+"F0.wireOp",EDGE,"E4.14.9.0"),sQuery(id+"F0.wireOp",EDGE,"E4.14.10.0"),sQuery(id+"F0.wireOp",EDGE,"E4.14.11.0"),sQuery(id+"F0.wireOp",EDGE,"E4.14.12.0"),sQuery(id+"F0.wireOp",EDGE,"E4.14.13.0"),sQuery(id+"F0.wireOp",EDGE,"E4.14.14.0")])],"isStart":false});
            var sketch = newSketch(context, id + "F2", { "sketchPlane" : qUnion([Q0])});
            skLineSegment(sketch, "E7.bottom", {"start": v(6.35, 401.7) * mm, "end": v(190.75, 401.7) * mm});
            skLineSegment(sketch, "E7.top", {"start": v(6.35, 376.3) * mm, "end": v(190.75, 376.3) * mm});
            skLineSegment(sketch, "E7.left", {"start": v(6.35, 401.7) * mm, "end": v(6.35, 376.3) * mm});
            skLineSegment(sketch, "E7.right", {"start": v(190.75, 401.7) * mm, "end": v(190.75, 376.3) * mm});
            skLineSegment(sketch, "E8", {"start": v(6.35, 389) * mm, "end": v(19.05, 389) * mm, "construction": true});
            skCircle(sketch, "E9", {"center": v(19.05, 389) * mm, "radius": 2.5 * mm});
            skLineSegment(sketch, "E10", {"start": v(190.75, 389) * mm, "end": v(178.05, 389) * mm, "construction": true});
            skCircle(sketch, "E11", {"center": v(178.05, 389) * mm, "radius": 2.5 * mm});
            skPoint(sketch, "E12", {"position": v(98.55, 401.7) * mm});
            skLineSegment(sketch, "E13", {"start": v(6.35, 401.7) * mm, "end": v(78.22, 401.7) * mm, "construction": true});
            skSolve(sketch);
        }
        {
            var Q0;
            {var subQ3=sQuery(id+"F2.wireOp",EDGE,"E7.top");Q0=makeQuery(id+"F2.imprint","IMPRINT",FACE,{"disambiguationData":[TD([[makeQuery(id+"F2.imprint","IMPRINT",EDGE,{"derivedFrom":subQ3}),-1.0]])]});}
            var sketch = newSketch(context, id + "F3", { "sketchPlane" : qUnion([Q0])});
            skLineSegment(sketch, "E14.bottom", {"start": v(137.05, 399.84) * mm, "end": v(162.45, 399.84) * mm});
            skLineSegment(sketch, "E14.top", {"start": v(137.05, 212.44) * mm, "end": v(162.45, 212.44) * mm});
            skLineSegment(sketch, "E14.left", {"start": v(137.05, 399.84) * mm, "end": v(137.05, 212.44) * mm});
            skLineSegment(sketch, "E14.right", {"start": v(162.45, 399.84) * mm, "end": v(162.45, 212.44) * mm});
            skLineSegment(sketch, "E15", {"start": v(149.75, 399.84) * mm, "end": v(149.75, 387.14) * mm, "construction": true});
            skLineSegment(sketch, "E16", {"start": v(149.75, 212.44) * mm, "end": v(149.75, 225.14) * mm, "construction": true});
            skCircle(sketch, "E17", {"center": v(149.75, 387.14) * mm, "radius": 2.5 * mm});
            skCircle(sketch, "E18", {"center": v(149.75, 225.14) * mm, "radius": 2.5 * mm});
            skSolve(sketch);
        }
        {
            var Q0;
            {var subQ3=sQuery(id+"F2.wireOp",EDGE,"E7.top");Q0=makeQuery(id+"F2.imprint","IMPRINT",FACE,{"disambiguationData":[TD([[makeQuery(id+"F2.imprint","IMPRINT",EDGE,{"derivedFrom":subQ3}),-1.0]])]});}
            var sketch = newSketch(context, id + "F4", { "sketchPlane" : qUnion([Q0])});
            skLineSegment(sketch, "E19.bottom", {"start": v(34.32, 412.34) * mm, "end": v(59.72, 412.34) * mm});
            skLineSegment(sketch, "E19.top", {"start": v(34.32, 249.94) * mm, "end": v(59.72, 249.94) * mm});
            skLineSegment(sketch, "E19.left", {"start": v(34.32, 412.34) * mm, "end": v(34.32, 249.94) * mm});
            skLineSegment(sketch, "E19.right", {"start": v(59.72, 412.34) * mm, "end": v(59.72, 249.94) * mm});
            skLineSegment(sketch, "E20", {"start": v(47.02, 412.34) * mm, "end": v(47.02, 399.64) * mm, "construction": true});
            skLineSegment(sketch, "E21", {"start": v(47.02, 249.94) * mm, "end": v(47.02, 262.64) * mm, "construction": true});
            skCircle(sketch, "E22", {"center": v(47.02, 399.64) * mm, "radius": 2.5 * mm});
            skCircle(sketch, "E23", {"center": v(47.02, 262.64) * mm, "radius": 2.5 * mm});
            skSolve(sketch);
        }
        {
            var Q0;
            Q0 = qSketchRegion(id + "F2", true);
            extrude(context, id + "F5", {"entities" : qUnion([Q0]), "depth" : 1.14 * mm});
        }
        {
            var Q0;
            Q0 = qSketchRegion(id + "F3", true);
            extrude(context, id + "F6", {"entities" : qUnion([Q0]), "depth" : 1.14 * mm});
        }
        {
            var Q0;
            Q0 = qSketchRegion(id + "F4", true);
            extrude(context, id + "F7", {"entities" : qUnion([Q0]), "depth" : 1.14 * mm});
        }
    });
